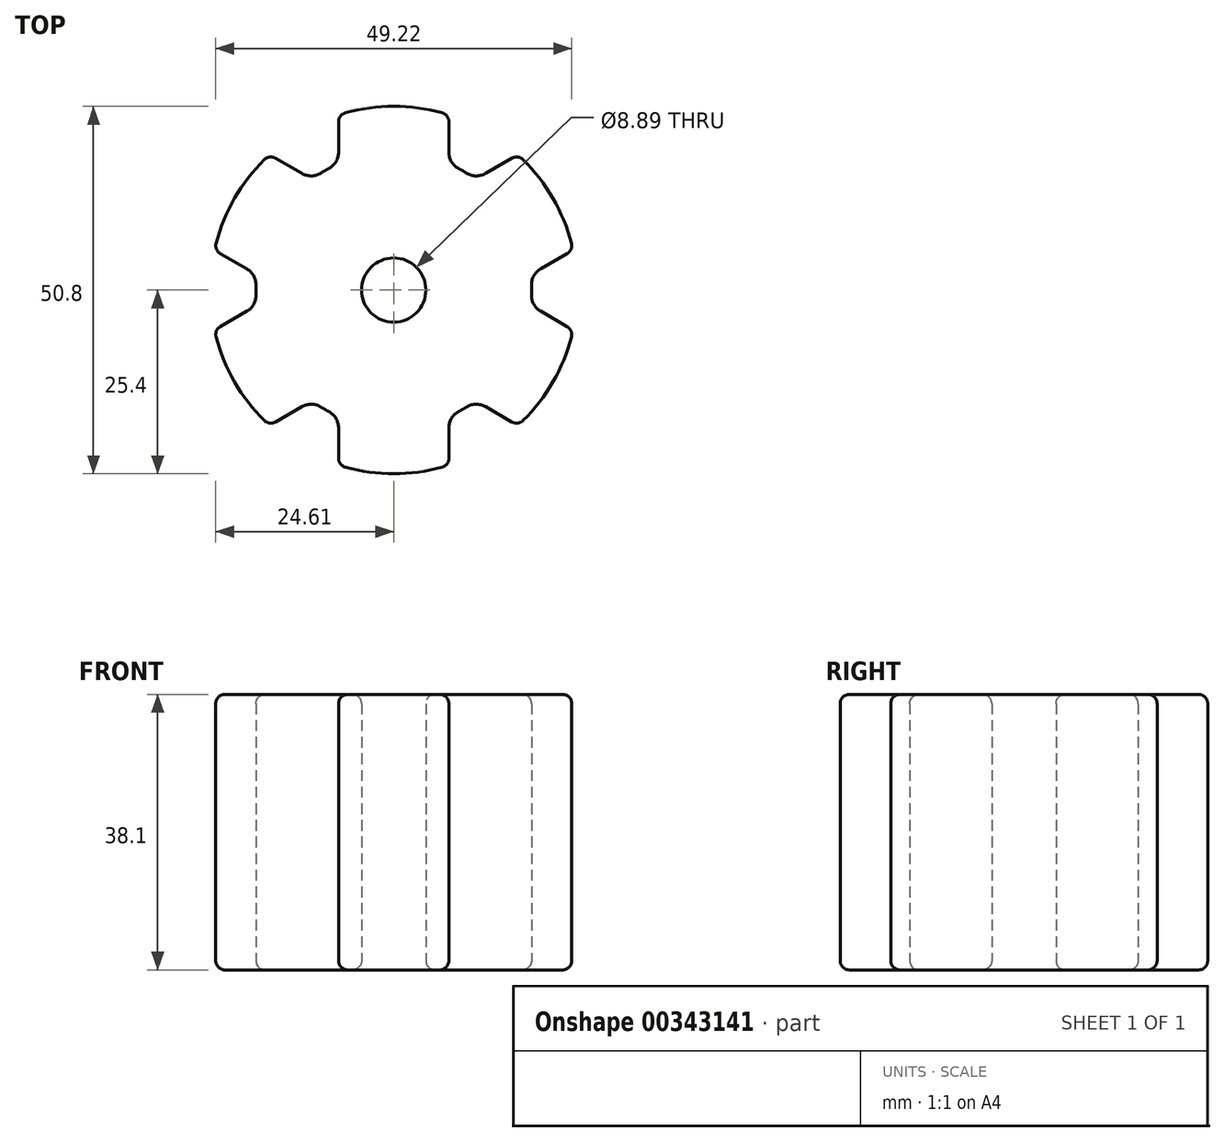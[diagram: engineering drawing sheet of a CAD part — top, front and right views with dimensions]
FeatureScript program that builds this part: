
annotation { "Feature Type Name" : "Feature", "Feature Type Description" : "" }
export const myFeature = defineFeature(function(context is Context, id is Id, definition is map)
    precondition{}
    {
        {
            var Q0;
            Q0=qCreatedBy(makeId("Top.planeOp"),FACE);
            var sketch = newSketch(context, id + "F0", { "sketchPlane" : qUnion([Q0])});
            skCircle(sketch, "E0", {"center": v(0, 0) * mm, "radius": 4.45 * mm});
            skArc(sketch, "E1", {"start": v(6.68, 24.5) * mm, "mid": v(0, 25.4) * mm, "end": v(-6.68, 24.5) * mm});
            skArc(sketch, "E2", {"start": v(-8.96, 16.8) * mm, "mid": v(0, -19.05) * mm, "end": v(8.96, 16.8) * mm});
            skLineSegment(sketch, "E3", {"start": v(0, 0) * mm, "end": v(0, 25.4) * mm, "construction": true});
            skLineSegment(sketch, "E4.left", {"start": v(-7.62, 19.05) * mm, "end": v(-7.62, 23.28) * mm});
            skLineSegment(sketch, "E4.right", {"start": v(7.62, 19.05) * mm, "end": v(7.62, 23.28) * mm});
            skPoint(sketch, "E5.visualSharp", {"position": v(-7.62, 24.23) * mm});
            skArc(sketch, "E5.filletArc", {"start": v(-6.68, 24.5) * mm, "mid": v(-7.36, 24.05) * mm, "end": v(-7.62, 23.28) * mm});
            skPoint(sketch, "E6.visualSharp", {"position": v(7.62, 24.23) * mm});
            skArc(sketch, "E6.filletArc", {"start": v(7.62, 23.28) * mm, "mid": v(7.36, 24.05) * mm, "end": v(6.68, 24.5) * mm});
            skPoint(sketch, "E7.visualSharp", {"position": v(-7.62, 17.46) * mm});
            skArc(sketch, "E7.filletArc", {"start": v(-8.96, 16.8) * mm, "mid": v(-7.98, 17.74) * mm, "end": v(-7.62, 19.05) * mm});
            skPoint(sketch, "E8.visualSharp", {"position": v(7.62, 17.46) * mm});
            skArc(sketch, "E8.filletArc", {"start": v(7.62, 19.05) * mm, "mid": v(7.98, 17.74) * mm, "end": v(8.96, 16.8) * mm});
            skArc(sketch, "E9.1.0", {"start": v(-19.04, 0.64) * mm, "mid": v(-19.36, 1.96) * mm, "end": v(-20.3, 2.93) * mm});
            skArc(sketch, "E9.1.1", {"start": v(-24.56, 6.46) * mm, "mid": v(-24.5, 5.65) * mm, "end": v(-23.97, 5.04) * mm});
            skLineSegment(sketch, "E9.1.2", {"start": v(-20.3, 2.93) * mm, "end": v(-23.97, 5.04) * mm});
            skArc(sketch, "E9.1.3", {"start": v(-17.88, 18.04) * mm, "mid": v(-22, 12.7) * mm, "end": v(-24.56, 6.46) * mm});
            skArc(sketch, "E9.1.4", {"start": v(-16.35, 18.24) * mm, "mid": v(-17.15, 18.4) * mm, "end": v(-17.88, 18.04) * mm});
            skLineSegment(sketch, "E9.1.5", {"start": v(-12.69, 16.12) * mm, "end": v(-16.35, 18.24) * mm});
            skArc(sketch, "E9.1.6", {"start": v(-12.69, 16.12) * mm, "mid": v(-11.38, 15.78) * mm, "end": v(-10.07, 16.17) * mm});
            skArc(sketch, "E9.2.0", {"start": v(-10.07, -16.17) * mm, "mid": v(-11.38, -15.78) * mm, "end": v(-12.69, -16.12) * mm});
            skArc(sketch, "E9.2.1", {"start": v(-17.88, -18.04) * mm, "mid": v(-17.15, -18.4) * mm, "end": v(-16.35, -18.24) * mm});
            skLineSegment(sketch, "E9.2.2", {"start": v(-12.69, -16.12) * mm, "end": v(-16.35, -18.24) * mm});
            skArc(sketch, "E9.2.3", {"start": v(-24.56, -6.46) * mm, "mid": v(-22, -12.7) * mm, "end": v(-17.88, -18.04) * mm});
            skArc(sketch, "E9.2.4", {"start": v(-23.97, -5.04) * mm, "mid": v(-24.5, -5.65) * mm, "end": v(-24.56, -6.46) * mm});
            skLineSegment(sketch, "E9.2.5", {"start": v(-20.3, -2.93) * mm, "end": v(-23.97, -5.04) * mm});
            skArc(sketch, "E9.2.6", {"start": v(-20.3, -2.93) * mm, "mid": v(-19.36, -1.96) * mm, "end": v(-19.04, -0.64) * mm});
            skArc(sketch, "E10.2.3.0", {"start": v(8.96, -16.8) * mm, "mid": v(7.98, -17.74) * mm, "end": v(7.62, -19.05) * mm});
            skArc(sketch, "E10.4.3.0", {"start": v(6.68, -24.5) * mm, "mid": v(7.36, -24.05) * mm, "end": v(7.62, -23.28) * mm});
            skLineSegment(sketch, "E10.8.3.0", {"start": v(7.62, -19.05) * mm, "end": v(7.62, -23.28) * mm});
            skArc(sketch, "E10.11.3.0", {"start": v(-6.68, -24.5) * mm, "mid": v(0, -25.4) * mm, "end": v(6.68, -24.5) * mm});
            skArc(sketch, "E10.15.3.0", {"start": v(-7.62, -23.28) * mm, "mid": v(-7.36, -24.05) * mm, "end": v(-6.68, -24.5) * mm});
            skLineSegment(sketch, "E10.19.3.0", {"start": v(-7.62, -19.05) * mm, "end": v(-7.62, -23.28) * mm});
            skArc(sketch, "E10.22.3.0", {"start": v(-7.62, -19.05) * mm, "mid": v(-7.98, -17.74) * mm, "end": v(-8.96, -16.8) * mm});
            skArc(sketch, "E10.2.4.0", {"start": v(19.04, -0.64) * mm, "mid": v(19.36, -1.96) * mm, "end": v(20.3, -2.93) * mm});
            skArc(sketch, "E10.4.4.0", {"start": v(24.56, -6.46) * mm, "mid": v(24.5, -5.65) * mm, "end": v(23.97, -5.04) * mm});
            skLineSegment(sketch, "E10.8.4.0", {"start": v(20.3, -2.93) * mm, "end": v(23.97, -5.04) * mm});
            skArc(sketch, "E10.11.4.0", {"start": v(17.88, -18.04) * mm, "mid": v(22, -12.7) * mm, "end": v(24.56, -6.46) * mm});
            skArc(sketch, "E10.15.4.0", {"start": v(16.35, -18.24) * mm, "mid": v(17.15, -18.4) * mm, "end": v(17.88, -18.04) * mm});
            skLineSegment(sketch, "E10.19.4.0", {"start": v(12.69, -16.12) * mm, "end": v(16.35, -18.24) * mm});
            skArc(sketch, "E10.22.4.0", {"start": v(12.69, -16.12) * mm, "mid": v(11.38, -15.78) * mm, "end": v(10.07, -16.17) * mm});
            skArc(sketch, "E11.2.5.0", {"start": v(10.07, 16.17) * mm, "mid": v(11.38, 15.78) * mm, "end": v(12.69, 16.12) * mm});
            skArc(sketch, "E11.4.5.0", {"start": v(17.88, 18.04) * mm, "mid": v(17.15, 18.4) * mm, "end": v(16.35, 18.24) * mm});
            skLineSegment(sketch, "E11.8.5.0", {"start": v(12.69, 16.12) * mm, "end": v(16.35, 18.24) * mm});
            skArc(sketch, "E11.11.5.0", {"start": v(24.56, 6.46) * mm, "mid": v(22, 12.7) * mm, "end": v(17.88, 18.04) * mm});
            skArc(sketch, "E11.15.5.0", {"start": v(23.97, 5.04) * mm, "mid": v(24.5, 5.65) * mm, "end": v(24.56, 6.46) * mm});
            skLineSegment(sketch, "E11.19.5.0", {"start": v(20.3, 2.93) * mm, "end": v(23.97, 5.04) * mm});
            skArc(sketch, "E11.22.5.0", {"start": v(20.3, 2.93) * mm, "mid": v(19.36, 1.96) * mm, "end": v(19.04, 0.64) * mm});
            skSolve(sketch);
        }
        {
            var Q0;
            Q0 = qSketchRegion(id + "F0", true);
            extrude(context, id + "F1", {"entities" : qUnion([Q0]), "depth" : 38.1 * mm});
        }
        {
            var Q0;
            Q0=makeQuery(id+"F1.opExtrude","CAP_FACE",FACE,{"disambiguationData":[OSD([sQuery(id+"F0.wireOp",EDGE,"E0"),sQuery(id+"F0.wireOp",EDGE,"E1")])],"isStart":false});
            var Q1;
            Q1=makeQuery(id+"F1.opExtrude","CAP_FACE",FACE,{"disambiguationData":[OSD([sQuery(id+"F0.wireOp",EDGE,"E0"),sQuery(id+"F0.wireOp",EDGE,"E1")])],"isStart":true});
            fillet(context, id + "F2", {"entities" : qUnion([Q0, Q1]), "radius" : 1.27 * mm, "tangentPropagation" : true, "allowEdgeOverflow" : false});
        }
    });
